# Revit family: 0032000
name_source: partatom
category: Lighting Fixtures
revit_build: Autodesk Revit 2017 (Build: 20190507_1515(x64)
units: mm (PartAtom-declared; Revit-internal decimal feet)

## family parameters
Cut with Voids When Loaded = No
Host = Face
Light Source = No
OmniClass Number = 23.80.70.00
OmniClass Title = Lighting
Part Type = Normal
Room Calculation Point = No
Round Connector Dimension = Use Diameter
Shared = No

## types (4) — shared parameters
Apparent Load = 2 VA
Assembly Code = D5020200
AssetType = Fixed
ClassificationName = Uniclass2015
ClassificationValue = EF_70_80
Default Elevation = 1219 mm
DimmingControlOptions = Non dimmable
DocumentationLiterature = http://www.sylvania-lighting.com
DurationUnit = hours
ElectricShockClassification = Class II
IfcExportAs = IfcLightFixtureType
IfcExportType = IfcLightFixtureType
ImpactProtectionIndex = IK02
IngressProtection = IP20
InputNominalFrequency = 50/60 Hz
InputVoltage = 220-240V~
Keynote = 16500
Lamp = LED
LampColourRenderingIndex = 70
LampColourTemperature = 6500 K
LampNominalLuminous = 24 lm
LampsType = LED
Length_SYL = 308 mm  [stored 1.0105 ft]
LuminousEfficacy = 12 lm/W
Manufacturer = Feilo Sylvania
ManufacturerName = Feilo Sylvania
Material_1_SYL = PC/ABS Plastic
Material_2_SYL = <By Category>
Material_3_SYL = <By Category>
Material_4_SYL = <By Category>
Model = START Emergency Exit Surface MT M 3h
ModelNumber = 0032000
ModelReference = START Emergency Exit Surface MT M 3h
Name = START Emergency Exit Surface MT M 3h
PowerConsumption = 2.0 W
PowerFactor = 0.49
RadiusBody_SYL = 17 mm  [stored 0.0557743 ft]
RotatableArmThickness_SYL = 3 mm  [stored 0.00984252 ft]
Type Image = <None>
TypeName = START Emergency Exit Surface MT M 3h
URL = http://www.sylvania-lighting.com
Voltage = 230 V
Width_SYL = 34 mm  [stored 0.111549 ft]
zero-valued in all types: Cost, NominalDepth, NominalHeight, NominalLength

## per-type parameters (varying)
| type | ArrowDirection_SYL |
| 0032000 START EM EXIT SURFACE MT M 3H Arrow Right | Tiltable EXIT Sign : Exit Arrow Right |
| 0032000 START EM EXIT SURFACE MT M 3H Arrow Left | Tiltable EXIT Sign : Exit Arrow Left |
| 0032000 START EM EXIT SURFACE MT M 3H Arrow Up | Tiltable EXIT Sign : Exit Arrow Up |
| 0032000 START EM EXIT SURFACE MT M 3H Arrow Down | Tiltable EXIT Sign : Exit Arrow Down |

note: [stored X ft] marks values corroborated as IEEE doubles in the binary element streams (Revit-internal decimal feet)

## geometry (parser evidence)
native form markers: Sweep x6
no freeform markers — native parametric forms only
